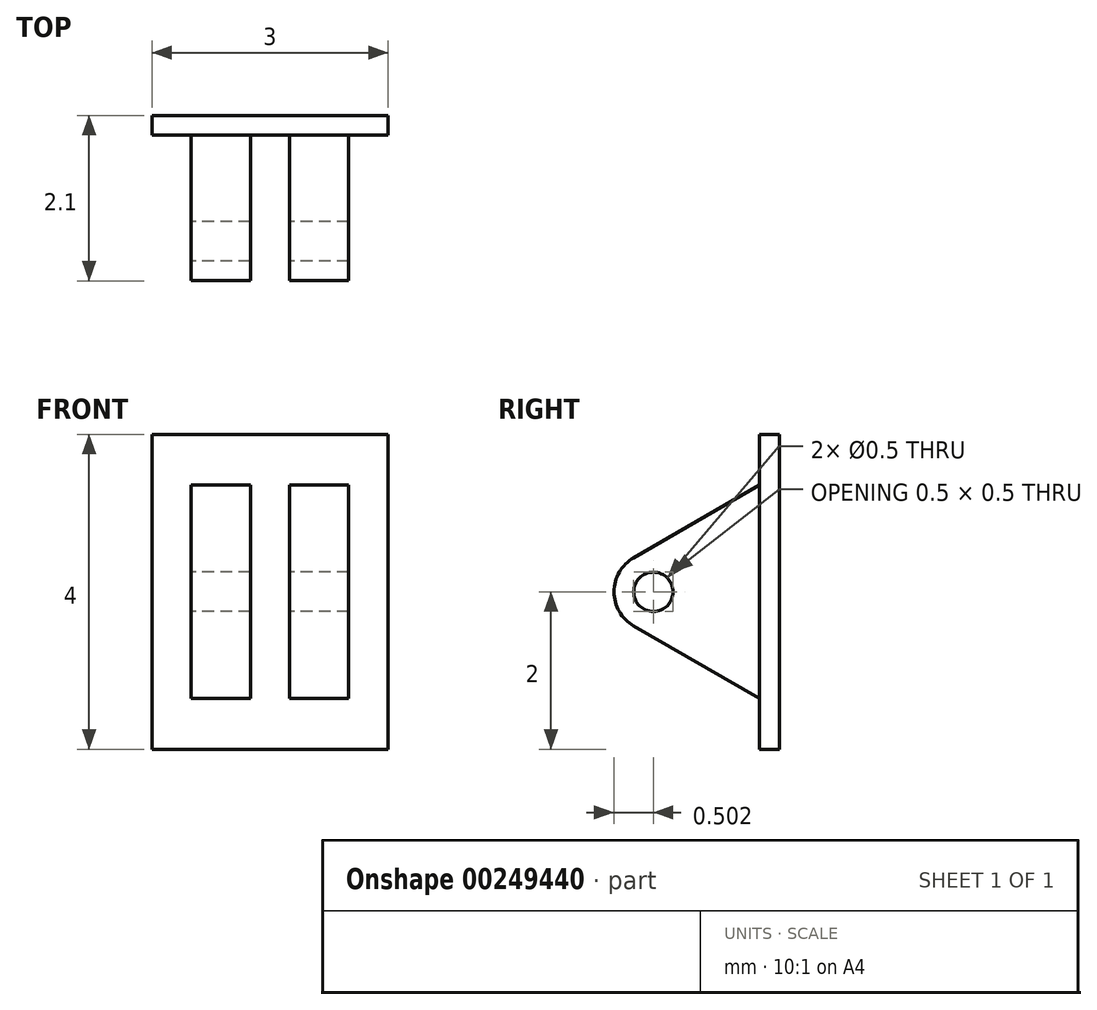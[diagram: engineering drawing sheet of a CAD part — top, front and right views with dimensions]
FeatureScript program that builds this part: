
annotation { "Feature Type Name" : "Feature", "Feature Type Description" : "" }
export const myFeature = defineFeature(function(context is Context, id is Id, definition is map)
    precondition{}
    {
        {
            var Q0;
            Q0=qCreatedBy(makeId("Front.planeOp"),FACE);
            var sketch = newSketch(context, id + "F0", { "sketchPlane" : qUnion([Q0])});
            skLineSegment(sketch, "E0.bottom", {"start": v(-1.5, 2) * mm, "end": v(1.5, 2) * mm});
            skLineSegment(sketch, "E0.top", {"start": v(-1.5, -2) * mm, "end": v(1.5, -2) * mm});
            skLineSegment(sketch, "E0.left", {"start": v(-1.5, 2) * mm, "end": v(-1.5, -2) * mm});
            skLineSegment(sketch, "E0.right", {"start": v(1.5, 2) * mm, "end": v(1.5, -2) * mm});
            skPoint(sketch, "E0.middle", {"position": v(0, 0) * mm});
            skSolve(sketch);
        }
        {
            var Q0;
            Q0 = qSketchRegion(id + "F0", true);
            extrude(context, id + "F1", {"entities" : qUnion([Q0]), "depth" : .250 * mm});
        }
        {
            var Q0;
            Q0=qCreatedBy(makeId("Right.planeOp"),FACE);
            var sketch = newSketch(context, id + "F2", { "sketchPlane" : qUnion([Q0])});
            skLineSegment(sketch, "E1", {"start": v(0, -1.5) * mm, "end": v(-1.85, -0.43) * mm});
            skLineSegment(sketch, "E2", {"start": v(-1.85, 0.43) * mm, "end": v(0, 1.5) * mm});
            skLineSegment(sketch, "E3", {"start": v(0, -1.5) * mm, "end": v(0, 1.5) * mm});
            skPoint(sketch, "E4", {"position": v(0, -1.5) * mm});
            skPoint(sketch, "E5", {"position": v(0, 1.5) * mm});
            skPoint(sketch, "E6.visualSharp", {"position": v(-2.6, 0) * mm});
            skArc(sketch, "E6.filletArc", {"start": v(-1.85, 0.43) * mm, "mid": v(-2.1, 0) * mm, "end": v(-1.85, -0.43) * mm});
            skCircle(sketch, "E7", {"center": v(-1.6, 0) * mm, "radius": 0.25 * mm});
            skSolve(sketch);
        }
        {
            var Q0;
            Q0=makeQuery(id+"F2.imprint","IMPRINT",FACE,{"disambiguationData":[TD([[makeQuery(id+"F2.imprint","IMPRINT",EDGE,{"derivedFrom":sQuery(id+"F2.wireOp",EDGE,"E1")}),-1.0]])]});
            extrude(context, id + "F3", {"entities" : qUnion([Q0]), "operationType" : NewBodyOperationType.ADD, "endBound" : BoundingType.SYMMETRIC, "depth" : 2 * mm});
        }
        {
            var Q0;
            Q0=qCreatedBy(makeId("Top.planeOp"),FACE);
            var sketch = newSketch(context, id + "F4", { "sketchPlane" : qUnion([Q0])});
            skLineSegment(sketch, "E8.bottom", {"start": v(-0.25, -0.25) * mm, "end": v(0.25, -0.25) * mm});
            skLineSegment(sketch, "E8.top", {"start": v(-0.25, -4.37) * mm, "end": v(0.25, -4.37) * mm});
            skLineSegment(sketch, "E8.left", {"start": v(-0.25, -0.25) * mm, "end": v(-0.25, -4.37) * mm});
            skLineSegment(sketch, "E8.right", {"start": v(0.25, -0.25) * mm, "end": v(0.25, -4.37) * mm});
            skPoint(sketch, "E8.middle", {"position": v(0, -2.31) * mm});
            skSolve(sketch);
        }
        {
            var Q0;
            Q0=makeQuery(id+"F4.imprint","IMPRINT",FACE,{"disambiguationData":[TD([[makeQuery(id+"F4.imprint","IMPRINT",EDGE,{"derivedFrom":sQuery(id+"F4.wireOp",EDGE,"E8.bottom")}),-1.0]])]});
            extrude(context, id + "F5", {"entities" : qUnion([Q0]), "operationType" : NewBodyOperationType.REMOVE, "endBound" : BoundingType.SYMMETRIC, "oppositeDirection" : true, "depth" : 25 * mm});
        }
    });
